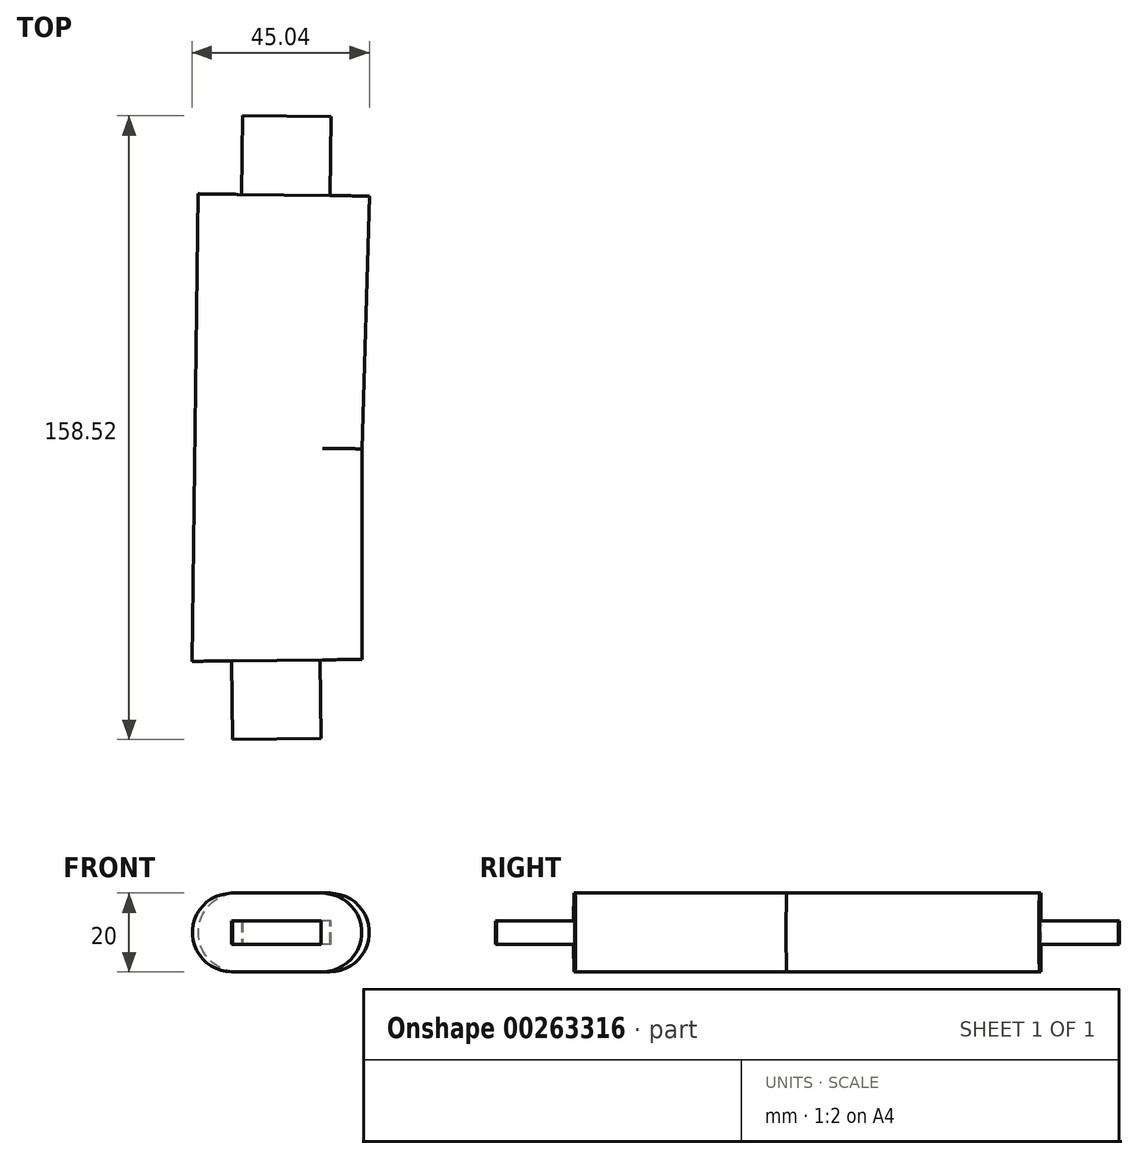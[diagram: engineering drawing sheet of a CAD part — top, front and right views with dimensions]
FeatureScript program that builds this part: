
annotation { "Feature Type Name" : "Feature", "Feature Type Description" : "" }
export const myFeature = defineFeature(function(context is Context, id is Id, definition is map)
    precondition{}
    {
        {
            var Q0;
            Q0=qCreatedBy(makeId("Top.planeOp"),FACE);
            var sketch = newSketch(context, id + "F0", { "sketchPlane" : qUnion([Q0])});
            skArc(sketch, "E0", {"start": v(-69.56, -48.3) * mm, "mid": v(-88.08, -45.25) * mm, "end": v(-106.8, -43.78) * mm});
            skArc(sketch, "E1", {"start": v(-106.8, -43.78) * mm, "mid": v(-96.39, -62.57) * mm, "end": v(-80.73, -77.27) * mm});
            skArc(sketch, "E2", {"start": v(-80.73, -77.27) * mm, "mid": v(-98.26, -84.7) * mm, "end": v(-114.23, -95.07) * mm});
            skArc(sketch, "E3", {"start": v(-114.23, -95.07) * mm, "mid": v(-98.6, -104.41) * mm, "end": v(-80.73, -107.98) * mm});
            skArc(sketch, "E4", {"start": v(-80.73, -107.98) * mm, "mid": v(-90.04, -123.58) * mm, "end": v(-94.69, -141.13) * mm});
            skArc(sketch, "E5", {"start": v(-94.69, -141.13) * mm, "mid": v(-78.8, -139.7) * mm, "end": v(-63.98, -133.8) * mm});
            skArc(sketch, "E6", {"start": v(-63.98, -133.8) * mm, "mid": v(40.14, -139.24) * mm, "end": v(30.94, -35.4) * mm});
            skArc(sketch, "E7", {"start": v(-31.41, -22.87) * mm, "mid": v(-53.17, -31.57) * mm, "end": v(-69.56, -48.3) * mm});
            skCircle(sketch, "E8", {"center": v(-12, -90) * mm, "radius": 35 * mm});
            skLineSegment(sketch, "E9", {"start": v(-12, -90) * mm, "end": v(-12, 0) * mm});
            skLineSegment(sketch, "E10", {"start": v(-12, 0) * mm, "end": v(0, 0) * mm});
            skLineSegment(sketch, "E11", {"start": v(-31.41, -22.87) * mm, "end": v(-12, 0) * mm});
            skLineSegment(sketch, "E12", {"start": v(-31.41, -22.87) * mm, "end": v(0, 0) * mm});
            skArc(sketch, "E13", {"start": v(30.94, -35.4) * mm, "mid": v(57.65, 8.29) * mm, "end": v(64.82, 58.99) * mm});
            skLineSegment(sketch, "E14", {"start": v(64.82, 42.9) * mm, "end": v(70.1, 125.75) * mm});
            skLineSegment(sketch, "E15", {"start": v(70.1, 125.75) * mm, "end": v(73.47, 146.99) * mm});
            skLineSegment(sketch, "E16", {"start": v(73.47, 146.99) * mm, "end": v(91.25, 150.97) * mm});
            skArc(sketch, "E17", {"start": v(93.55, 168.05) * mm, "mid": v(98.13, 170.3) * mm, "end": v(101.04, 174.5) * mm});
            skArc(sketch, "E18", {"start": v(101.04, 174.5) * mm, "mid": v(98.19, 178.86) * mm, "end": v(93.55, 181.22) * mm});
            skArc(sketch, "E19", {"start": v(91.25, 150.97) * mm, "mid": v(97.19, 153.5) * mm, "end": v(101.85, 157.96) * mm});
            skArc(sketch, "E20", {"start": v(101.85, 157.96) * mm, "mid": v(99.5, 164.5) * mm, "end": v(93.55, 168.05) * mm});
            skArc(sketch, "E21", {"start": v(93.55, 181.22) * mm, "mid": v(100.45, 185.24) * mm, "end": v(104.38, 192.2) * mm});
            skArc(sketch, "E22", {"start": v(16.27, 5.35) * mm, "mid": v(27.94, 20.47) * mm, "end": v(35.96, 37.8) * mm});
            skLineSegment(sketch, "E23", {"start": v(16.27, 5.35) * mm, "end": v(12.02, 0.97) * mm});
            skLineSegment(sketch, "E24", {"start": v(12.02, 54.47) * mm, "end": v(16.98, 220.58) * mm});
            skLineSegment(sketch, "E25", {"start": v(16.98, 220.58) * mm, "end": v(16.98, 230.48) * mm});
            skArc(sketch, "E26", {"start": v(20.74, 234.78) * mm, "mid": v(18.05, 233.34) * mm, "end": v(16.98, 230.48) * mm});
            skLineSegment(sketch, "E27", {"start": v(20.74, 234.78) * mm, "end": v(55.67, 234.78) * mm});
            skArc(sketch, "E28", {"start": v(55.67, 234.78) * mm, "mid": v(75.45, 242.82) * mm, "end": v(84, 262.38) * mm});
            skArc(sketch, "E29", {"start": v(84, 262.38) * mm, "mid": v(83.8, 275) * mm, "end": v(79.59, 286.9) * mm});
            skArc(sketch, "E30", {"start": v(79.59, 286.9) * mm, "mid": v(90.12, 305.47) * mm, "end": v(96.46, 325.87) * mm});
            skArc(sketch, "E31", {"start": v(96.46, 325.87) * mm, "mid": v(80.34, 314.22) * mm, "end": v(65.52, 300.95) * mm});
            skArc(sketch, "E32", {"start": v(65.52, 300.95) * mm, "mid": v(66.02, 314.82) * mm, "end": v(65.52, 328.68) * mm});
            skArc(sketch, "E33", {"start": v(41.86, 304.54) * mm, "mid": v(40.03, 315.53) * mm, "end": v(35.9, 325.87) * mm});
            skArc(sketch, "E34", {"start": v(35.9, 325.87) * mm, "mid": v(29.68, 316.4) * mm, "end": v(23.68, 306.81) * mm});
            skArc(sketch, "E35", {"start": v(23.68, 306.81) * mm, "mid": v(-21.12, 284.92) * mm, "end": v(-28, 235.53) * mm});
            skLineSegment(sketch, "E36", {"start": v(-31.41, -22.87) * mm, "end": v(-28, 235.53) * mm});
            skLineSegment(sketch, "E37", {"start": v(0, 0) * mm, "end": v(0, 302.13) * mm});
            skLineSegment(sketch, "E38", {"start": v(12.02, 0.97) * mm, "end": v(-31.41, -22.87) * mm});
            skLineSegment(sketch, "E39", {"start": v(0, 0) * mm, "end": v(12.02, 0.97) * mm});
            skLineSegment(sketch, "E40", {"start": v(12.02, 0.97) * mm, "end": v(30.94, -35.4) * mm});
            skLineSegment(sketch, "E41", {"start": v(64.82, 58.99) * mm, "end": v(46.6, 104.17) * mm});
            skLineSegment(sketch, "E42", {"start": v(12.02, 0.97) * mm, "end": v(12.02, 54.47) * mm});
            skLineSegment(sketch, "E43", {"start": v(-29.54, 119.27) * mm, "end": v(13.94, 118.7) * mm});
            skLineSegment(sketch, "E44", {"start": v(35.96, 37.8) * mm, "end": v(38.97, 138.47) * mm});
            skArc(sketch, "E45", {"start": v(104.38, 192.2) * mm, "mid": v(74.78, 206.52) * mm, "end": v(46.71, 189.39) * mm});
            skArc(sketch, "E46", {"start": v(46.71, 189.39) * mm, "mid": v(41.3, 164.16) * mm, "end": v(38.97, 138.47) * mm});
            skLineSegment(sketch, "E47", {"start": v(104.38, 192.2) * mm, "end": v(93.55, 181.22) * mm});
            skLineSegment(sketch, "E48", {"start": v(93.55, 168.05) * mm, "end": v(101.85, 157.96) * mm});
            skLineSegment(sketch, "E49", {"start": v(93.55, 181.22) * mm, "end": v(101.04, 174.5) * mm});
            skLineSegment(sketch, "E50", {"start": v(93.55, 168.05) * mm, "end": v(101.04, 174.5) * mm});
            skLineSegment(sketch, "E51", {"start": v(41.86, 304.54) * mm, "end": v(65.52, 328.68) * mm});
            skLineSegment(sketch, "E52", {"start": v(16.98, 230.48) * mm, "end": v(-28.07, 230.48) * mm});
            skLineSegment(sketch, "E53", {"start": v(12.02, 0.97) * mm, "end": v(-31.1, 0.49) * mm});
            skPoint(sketch, "E53.endSnap0", {"position": v(6.01, 0.49) * mm});
            skLineSegment(sketch, "E54", {"start": v(12.02, 0.97) * mm, "end": v(43.15, -20.17) * mm});
            skSolve(sketch);
        }
        {
            var Q0;
            {var subQ0=sQuery(id+"F0.wireOp",EDGE,"E38");var subQ1=sQuery(id+"F0.wireOp",EDGE,"E9");var subQ2=makeQuery(id+"F0.imprint","INTERSECT",VERTEX,{"derivedFrom":[subQ1,subQ0]});Q0=makeQuery(id+"F0.imprint","IMPRINT",FACE,{"disambiguationData":[TD([[makeQuery(id+"F0.imprint","IMPRINT",EDGE,{"disambiguationData":[TD([[subQ2,-1.0]])],"derivedFrom":subQ1}),1.0]])]});}
            var Q1;
            {var subQ0=sQuery(id+"F0.wireOp",EDGE,"E11");Q1=makeQuery(id+"F0.imprint","IMPRINT",FACE,{"disambiguationData":[TD([[makeQuery(id+"F0.imprint","IMPRINT",EDGE,{"derivedFrom":subQ0}),-1.0]])]});}
            var Q2;
            {var subQ0=sQuery(id+"F0.wireOp",EDGE,"E39");Q2=makeQuery(id+"F0.imprint","IMPRINT",FACE,{"disambiguationData":[TD([[makeQuery(id+"F0.imprint","IMPRINT",EDGE,{"derivedFrom":subQ0}),1.0]])]});}
            var Q3;
            Q3=makeQuery(id+"F0.imprint","IMPRINT",FACE,{"disambiguationData":[TD([[makeQuery(id+"F0.imprint","IMPRINT",EDGE,{"derivedFrom":sQuery(id+"F0.wireOp",EDGE,"E0")}),1.0]])]});
            var Q4;
            {var subQ5=sQuery(id+"F0.wireOp",EDGE,"E39");Q4=makeQuery(id+"F0.imprint","IMPRINT",FACE,{"disambiguationData":[TD([[makeQuery(id+"F0.imprint","IMPRINT",EDGE,{"derivedFrom":subQ5}),-1.0]])]});}
            var Q5;
            {var subQ2=sQuery(id+"F0.wireOp",EDGE,"E10");Q5=makeQuery(id+"F0.imprint","IMPRINT",FACE,{"disambiguationData":[TD([[makeQuery(id+"F0.imprint","IMPRINT",EDGE,{"derivedFrom":subQ2}),1.0]])]});}
            var Q6;
            {var subQ0=sQuery(id+"F0.wireOp",EDGE,"E10");Q6=makeQuery(id+"F0.imprint","IMPRINT",FACE,{"disambiguationData":[TD([[makeQuery(id+"F0.imprint","IMPRINT",EDGE,{"derivedFrom":subQ0}),-1.0]])]});}
            var Q7;
            {var subQ0=sQuery(id+"F0.wireOp",EDGE,"E40");Q7=makeQuery(id+"F0.imprint","IMPRINT",FACE,{"disambiguationData":[TD([[makeQuery(id+"F0.imprint","IMPRINT",EDGE,{"derivedFrom":subQ0}),1.0]])]});}
            extrude(context, id + "F1", {"entities" : qUnion([Q0, Q1, Q2, Q3, Q4, Q5, Q6, Q7]), "depth" : 20 * mm});
        }
        {
            var Q0;
            {var subQ1=sQuery(id+"F0.wireOp",EDGE,"E14");Q0=makeQuery(id+"F0.imprint","IMPRINT",FACE,{"disambiguationData":[TD([[makeQuery(id+"F0.imprint","IMPRINT",EDGE,{"derivedFrom":subQ1}),1.0]])]});}
            extrude(context, id + "F2", {"entities" : qUnion([Q0]), "depth" : 20 * mm});
        }
        {
            var Q0;
            {var subQ0=sQuery(id+"F0.wireOp",EDGE,"E43");var subQ1=sQuery(id+"F0.wireOp",EDGE,"E36");var subQ2=makeQuery(id+"F0.imprint","INTERSECT",VERTEX,{"derivedFrom":[subQ1,subQ0]});Q0=makeQuery(id+"F0.imprint","IMPRINT",FACE,{"disambiguationData":[TD([[makeQuery(id+"F0.imprint","IMPRINT",EDGE,{"disambiguationData":[TD([[subQ2,1.0]])],"derivedFrom":subQ1}),-1.0]])]});}
            var Q1;
            {var subQ5=sQuery(id+"F0.wireOp",EDGE,"E42");Q1=makeQuery(id+"F0.imprint","IMPRINT",FACE,{"disambiguationData":[TD([[makeQuery(id+"F0.imprint","IMPRINT",EDGE,{"derivedFrom":subQ5}),1.0]])]});}
            extrude(context, id + "F3", {"entities" : qUnion([Q0, Q1]), "depth" : 20 * mm});
        }
        {
            var Q0;
            {var subQ0=sQuery(id+"F0.wireOp",EDGE,"E36");var subQ1=sQuery(id+"F0.wireOp",EDGE,"E35");var subQ2=makeQuery(id+"F0.imprint","INTERSECT",VERTEX,{"derivedFrom":[subQ1,subQ0]});Q0=makeQuery(id+"F0.imprint","IMPRINT",FACE,{"disambiguationData":[TD([[makeQuery(id+"F0.imprint","IMPRINT",EDGE,{"disambiguationData":[TD([[subQ2,1.0]])],"derivedFrom":subQ1}),1.0]])]});}
            var Q1;
            {var subQ4=sQuery(id+"F0.wireOp",EDGE,"E26");Q1=makeQuery(id+"F0.imprint","IMPRINT",FACE,{"disambiguationData":[TD([[makeQuery(id+"F0.imprint","IMPRINT",EDGE,{"derivedFrom":subQ4}),-1.0]])]});}
            extrude(context, id + "F4", {"entities" : qUnion([Q0, Q1]), "depth" : 20 * mm});
        }
        {
            var Q0;
            {var subQ0=sQuery(id+"F0.wireOp",EDGE,"E43");var subQ1=sQuery(id+"F0.wireOp",EDGE,"E36");var subQ2=makeQuery(id+"F0.imprint","INTERSECT",VERTEX,{"derivedFrom":[subQ1,subQ0]});Q0=makeQuery(id+"F0.imprint","IMPRINT",FACE,{"disambiguationData":[TD([[makeQuery(id+"F0.imprint","IMPRINT",EDGE,{"disambiguationData":[TD([[subQ2,-1.0]])],"derivedFrom":subQ1}),-1.0]])]});}
            var Q1;
            {var subQ7=sQuery(id+"F0.wireOp",EDGE,"E25");Q1=makeQuery(id+"F0.imprint","IMPRINT",FACE,{"disambiguationData":[TD([[makeQuery(id+"F0.imprint","IMPRINT",EDGE,{"derivedFrom":subQ7}),1.0]])]});}
            extrude(context, id + "F5", {"entities" : qUnion([Q0, Q1]), "depth" : 20 * mm});
        }
        {
            var Q0;
            Q0=makeQuery(id+"F1.opExtrude","CAP_EDGE",EDGE,{"disambiguationData":[OSD([sQuery(id+"F0.wireOp",EDGE,"E36")])],"isStart":false});
            var Q1;
            Q1=makeQuery(id+"F1.opExtrude","CAP_EDGE",EDGE,{"disambiguationData":[OSD([sQuery(id+"F0.wireOp",EDGE,"E24")])],"isStart":false});
            var Q2;
            Q2=makeQuery(id+"F1.opExtrude","CAP_EDGE",EDGE,{"disambiguationData":[OSD([sQuery(id+"F0.wireOp",EDGE,"E42")])],"isStart":false});
            var Q3;
            Q3=makeQuery(id+"F1.opExtrude","CAP_EDGE",EDGE,{"disambiguationData":[OSD([sQuery(id+"F0.wireOp",EDGE,"E25")])],"isStart":false});
            var Q4;
            Q4=makeQuery(id+"F1.opExtrude","CAP_EDGE",EDGE,{"disambiguationData":[OSD([sQuery(id+"F0.wireOp",EDGE,"E35")])],"isStart":false});
            var Q5;
            Q5=makeQuery(id+"F1.opExtrude","CAP_EDGE",EDGE,{"disambiguationData":[OSD([sQuery(id+"F0.wireOp",EDGE,"E26")])],"isStart":false});
            var Q6;
            Q6=makeQuery(id+"F1.opExtrude","CAP_EDGE",EDGE,{"disambiguationData":[OSD([sQuery(id+"F0.wireOp",EDGE,"E42")])],"isStart":true});
            var Q7;
            Q7=makeQuery(id+"F1.opExtrude","CAP_EDGE",EDGE,{"disambiguationData":[OSD([sQuery(id+"F0.wireOp",EDGE,"E25")])],"isStart":true});
            var Q8;
            Q8=makeQuery(id+"F1.opExtrude","CAP_EDGE",EDGE,{"disambiguationData":[OSD([sQuery(id+"F0.wireOp",EDGE,"E36")])],"isStart":true});
            var Q9;
            Q9=makeQuery(id+"F1.opExtrude","CAP_EDGE",EDGE,{"disambiguationData":[OSD([sQuery(id+"F0.wireOp",EDGE,"E35")])],"isStart":true});
            var Q10;
            Q10=makeQuery(id+"F1.opExtrude","CAP_EDGE",EDGE,{"disambiguationData":[OSD([sQuery(id+"F0.wireOp",EDGE,"E26")])],"isStart":true});
            var Q11;
            Q11=makeQuery(id+"F1.opExtrude","CAP_EDGE",EDGE,{"disambiguationData":[OSD([sQuery(id+"F0.wireOp",EDGE,"E22")])],"isStart":false});
            var Q12;
            Q12=makeQuery(id+"F1.opExtrude","CAP_EDGE",EDGE,{"disambiguationData":[OSD([sQuery(id+"F0.wireOp",EDGE,"E23")])],"isStart":false});
            var Q13;
            Q13=makeQuery(id+"F1.opExtrude","CAP_EDGE",EDGE,{"disambiguationData":[OSD([sQuery(id+"F0.wireOp",EDGE,"E44")])],"isStart":false});
            var Q14;
            Q14=makeQuery(id+"F1.opExtrude","CAP_EDGE",EDGE,{"disambiguationData":[OSD([sQuery(id+"F0.wireOp",EDGE,"E45")])],"isStart":false});
            var Q15;
            Q15=makeQuery(id+"F1.opExtrude","CAP_EDGE",EDGE,{"disambiguationData":[OSD([sQuery(id+"F0.wireOp",EDGE,"E22")])],"isStart":true});
            var Q16;
            Q16=makeQuery(id+"F1.opExtrude","CAP_EDGE",EDGE,{"disambiguationData":[OSD([sQuery(id+"F0.wireOp",EDGE,"E44")])],"isStart":true});
            var Q17;
            Q17=makeQuery(id+"F1.opExtrude","CAP_EDGE",EDGE,{"disambiguationData":[OSD([sQuery(id+"F0.wireOp",EDGE,"E45")])],"isStart":true});
            var Q18;
            Q18=makeQuery(id+"F1.opExtrude","CAP_EDGE",EDGE,{"disambiguationData":[OSD([sQuery(id+"F0.wireOp",EDGE,"E13")])],"isStart":false});
            var Q19;
            Q19=makeQuery(id+"F1.opExtrude","CAP_EDGE",EDGE,{"disambiguationData":[OSD([sQuery(id+"F0.wireOp",EDGE,"E14")])],"isStart":false});
            var Q20;
            Q20=makeQuery(id+"F1.opExtrude","CAP_EDGE",EDGE,{"disambiguationData":[OSD([sQuery(id+"F0.wireOp",EDGE,"E15")])],"isStart":false});
            var Q21;
            Q21=makeQuery(id+"F1.opExtrude","CAP_EDGE",EDGE,{"disambiguationData":[OSD([sQuery(id+"F0.wireOp",EDGE,"E16")])],"isStart":false});
            var Q22;
            Q22=makeQuery(id+"F1.opExtrude","CAP_EDGE",EDGE,{"disambiguationData":[OSD([sQuery(id+"F0.wireOp",EDGE,"E16")])],"isStart":true});
            var Q23;
            Q23=makeQuery(id+"F1.opExtrude","CAP_EDGE",EDGE,{"disambiguationData":[OSD([sQuery(id+"F0.wireOp",EDGE,"E15")])],"isStart":true});
            var Q24;
            Q24=makeQuery(id+"F1.opExtrude","CAP_EDGE",EDGE,{"disambiguationData":[OSD([sQuery(id+"F0.wireOp",EDGE,"E14")])],"isStart":true});
            var Q25;
            Q25=makeQuery(id+"F1.opExtrude","CAP_EDGE",EDGE,{"disambiguationData":[OSD([sQuery(id+"F0.wireOp",EDGE,"E13")])],"isStart":true});
            var Q26;
            Q26=makeQuery(id+"F1.opExtrude","CAP_EDGE",EDGE,{"disambiguationData":[OSD([sQuery(id+"F0.wireOp",EDGE,"E6")])],"isStart":false});
            var Q27;
            Q27=makeQuery(id+"F1.opExtrude","CAP_EDGE",EDGE,{"disambiguationData":[OSD([sQuery(id+"F0.wireOp",EDGE,"E8")])],"isStart":false});
            var Q28;
            Q28=makeQuery(id+"F1.opExtrude","CAP_EDGE",EDGE,{"disambiguationData":[OSD([sQuery(id+"F0.wireOp",EDGE,"E7")])],"isStart":false});
            var Q29;
            Q29=makeQuery(id+"F1.opExtrude","CAP_EDGE",EDGE,{"disambiguationData":[OSD([sQuery(id+"F0.wireOp",EDGE,"E8")])],"isStart":true});
            var Q30;
            Q30=makeQuery(id+"F1.opExtrude","CAP_EDGE",EDGE,{"disambiguationData":[OSD([sQuery(id+"F0.wireOp",EDGE,"E7")])],"isStart":true});
            var Q31;
            Q31=makeQuery(id+"F1.opExtrude","CAP_EDGE",EDGE,{"disambiguationData":[OSD([sQuery(id+"F0.wireOp",EDGE,"E6")])],"isStart":true});
            fillet(context, id + "F6", {"entities" : qUnion([Q0, Q1, Q2, Q3, Q4, Q5, Q6, Q7, Q8, Q9, Q10, Q11, Q12, Q13, Q14, Q15, Q16, Q17, Q18, Q19, Q20, Q21, Q22, Q23, Q24, Q25, Q26, Q27, Q28, Q29, Q30, Q31]), "radius" : 10 * mm, "tangentPropagation" : true, "allowEdgeOverflow" : false});
        }
        {
            var Q0;
            Q0=makeQuery(id+"F1.opExtrude","CAP_EDGE",EDGE,{"disambiguationData":[OSD([sQuery(id+"F0.wireOp",EDGE,"E0")])],"isStart":false});
            var Q1;
            Q1=makeQuery(id+"F1.opExtrude","CAP_EDGE",EDGE,{"disambiguationData":[OSD([sQuery(id+"F0.wireOp",EDGE,"E1")])],"isStart":false});
            var Q2;
            Q2=makeQuery(id+"F1.opExtrude","CAP_EDGE",EDGE,{"disambiguationData":[OSD([sQuery(id+"F0.wireOp",EDGE,"E5")])],"isStart":false});
            var Q3;
            Q3=makeQuery(id+"F1.opExtrude","CAP_EDGE",EDGE,{"disambiguationData":[OSD([sQuery(id+"F0.wireOp",EDGE,"E4")])],"isStart":false});
            var Q4;
            Q4=makeQuery(id+"F1.opExtrude","CAP_EDGE",EDGE,{"disambiguationData":[OSD([sQuery(id+"F0.wireOp",EDGE,"E0")])],"isStart":true});
            var Q5;
            Q5=makeQuery(id+"F1.opExtrude","CAP_EDGE",EDGE,{"disambiguationData":[OSD([sQuery(id+"F0.wireOp",EDGE,"E1")])],"isStart":true});
            var Q6;
            Q6=makeQuery(id+"F1.opExtrude","CAP_EDGE",EDGE,{"disambiguationData":[OSD([sQuery(id+"F0.wireOp",EDGE,"E4")])],"isStart":true});
            var Q7;
            Q7=makeQuery(id+"F1.opExtrude","CAP_EDGE",EDGE,{"disambiguationData":[OSD([sQuery(id+"F0.wireOp",EDGE,"E5")])],"isStart":true});
            fillet(context, id + "F7", {"entities" : qUnion([Q0, Q1, Q2, Q3, Q4, Q5, Q6, Q7]), "radius" : 9.5 * mm, "tangentPropagation" : true, "rho" : 0.5, "crossSection" : FilletCrossSection.CONIC, "allowEdgeOverflow" : false});
        }
        {
            var Q0;
            Q0=makeQuery(id+"F1.opExtrude","CAP_EDGE",EDGE,{"disambiguationData":[OSD([sQuery(id+"F0.wireOp",EDGE,"E3")])],"isStart":true});
            var Q1;
            Q1=makeQuery(id+"F1.opExtrude","CAP_EDGE",EDGE,{"disambiguationData":[OSD([sQuery(id+"F0.wireOp",EDGE,"E2")])],"isStart":true});
            var Q2;
            Q2=makeQuery(id+"F1.opExtrude","CAP_EDGE",EDGE,{"disambiguationData":[OSD([sQuery(id+"F0.wireOp",EDGE,"E2")])],"isStart":false});
            var Q3;
            Q3=makeQuery(id+"F1.opExtrude","CAP_EDGE",EDGE,{"disambiguationData":[OSD([sQuery(id+"F0.wireOp",EDGE,"E3")])],"isStart":false});
            fillet(context, id + "F8", {"entities" : qUnion([Q0, Q1, Q2, Q3]), "radius" : 3 * mm, "tangentPropagation" : true, "allowEdgeOverflow" : false});
        }
        {
            var Q0;
            Q0=makeQuery(id+"F2.opExtrude","CAP_EDGE",EDGE,{"disambiguationData":[OSD([sQuery(id+"F0.wireOp",EDGE,"E14")])],"isStart":false});
            var Q1;
            Q1=makeQuery(id+"F2.opExtrude","CAP_EDGE",EDGE,{"disambiguationData":[OSD([sQuery(id+"F0.wireOp",EDGE,"E15")])],"isStart":false});
            var Q2;
            Q2=makeQuery(id+"F2.opExtrude","CAP_EDGE",EDGE,{"disambiguationData":[OSD([sQuery(id+"F0.wireOp",EDGE,"E14")])],"isStart":true});
            var Q3;
            Q3=makeQuery(id+"F2.opExtrude","CAP_EDGE",EDGE,{"disambiguationData":[OSD([sQuery(id+"F0.wireOp",EDGE,"E15")])],"isStart":true});
            var Q4;
            Q4=makeQuery(id+"F2.opExtrude","CAP_EDGE",EDGE,{"disambiguationData":[OSD([sQuery(id+"F0.wireOp",EDGE,"E16")])],"isStart":true});
            var Q5;
            Q5=makeQuery(id+"F2.opExtrude","CAP_EDGE",EDGE,{"disambiguationData":[OSD([sQuery(id+"F0.wireOp",EDGE,"E16")])],"isStart":false});
            var Q6;
            Q6=makeQuery(id+"F2.opExtrude","CAP_EDGE",EDGE,{"disambiguationData":[OSD([sQuery(id+"F0.wireOp",EDGE,"E45")])],"isStart":true});
            var Q7;
            Q7=makeQuery(id+"F2.opExtrude","CAP_EDGE",EDGE,{"disambiguationData":[OSD([sQuery(id+"F0.wireOp",EDGE,"E45")])],"isStart":false});
            var Q8;
            Q8=makeQuery(id+"F2.opExtrude","CAP_EDGE",EDGE,{"disambiguationData":[OSD([sQuery(id+"F0.wireOp",EDGE,"E46")])],"isStart":false});
            var Q9;
            Q9=makeQuery(id+"F2.opExtrude","CAP_EDGE",EDGE,{"disambiguationData":[OSD([sQuery(id+"F0.wireOp",EDGE,"E44")])],"isStart":false});
            var Q10;
            Q10=makeQuery(id+"F2.opExtrude","CAP_EDGE",EDGE,{"disambiguationData":[OSD([sQuery(id+"F0.wireOp",EDGE,"E22")])],"isStart":false});
            var Q11;
            Q11=makeQuery(id+"F2.opExtrude","CAP_EDGE",EDGE,{"disambiguationData":[OSD([sQuery(id+"F0.wireOp",EDGE,"E23")])],"isStart":false});
            var Q12;
            Q12=makeQuery(id+"F2.opExtrude","CAP_EDGE",EDGE,{"disambiguationData":[OSD([sQuery(id+"F0.wireOp",EDGE,"E46")])],"isStart":true});
            var Q13;
            Q13=makeQuery(id+"F2.opExtrude","CAP_EDGE",EDGE,{"disambiguationData":[OSD([sQuery(id+"F0.wireOp",EDGE,"E23")])],"isStart":true});
            var Q14;
            Q14=makeQuery(id+"F2.opExtrude","CAP_EDGE",EDGE,{"disambiguationData":[OSD([sQuery(id+"F0.wireOp",EDGE,"E22")])],"isStart":true});
            var Q15;
            Q15=makeQuery(id+"F2.opExtrude","CAP_EDGE",EDGE,{"disambiguationData":[OSD([sQuery(id+"F0.wireOp",EDGE,"E44")])],"isStart":true});
            var Q16;
            Q16=makeQuery(id+"F3.opExtrude","CAP_EDGE",EDGE,{"disambiguationData":[OSD([sQuery(id+"F0.wireOp",EDGE,"E24")])],"isStart":false});
            var Q17;
            Q17=makeQuery(id+"F3.opExtrude","CAP_EDGE",EDGE,{"disambiguationData":[OSD([sQuery(id+"F0.wireOp",EDGE,"E42")])],"isStart":false});
            var Q18;
            Q18=makeQuery(id+"F3.opExtrude","CAP_EDGE",EDGE,{"disambiguationData":[OSD([sQuery(id+"F0.wireOp",EDGE,"E42")])],"isStart":true});
            var Q19;
            Q19=makeQuery(id+"F3.opExtrude","CAP_EDGE",EDGE,{"disambiguationData":[OSD([sQuery(id+"F0.wireOp",EDGE,"E24")])],"isStart":true});
            var Q20;
            Q20=makeQuery(id+"F3.opExtrude","CAP_EDGE",EDGE,{"disambiguationData":[OSD([sQuery(id+"F0.wireOp",EDGE,"E25")])],"isStart":true});
            var Q21;
            Q21=makeQuery(id+"F3.opExtrude","CAP_EDGE",EDGE,{"disambiguationData":[OSD([sQuery(id+"F0.wireOp",EDGE,"E36")])],"isStart":false});
            var Q22;
            Q22=makeQuery(id+"F3.opExtrude","CAP_EDGE",EDGE,{"disambiguationData":[OSD([sQuery(id+"F0.wireOp",EDGE,"E36")])],"isStart":true});
            var Q23;
            Q23=makeQuery(id+"F4.opExtrude","CAP_EDGE",EDGE,{"disambiguationData":[OSD([sQuery(id+"F0.wireOp",EDGE,"E36")])],"isStart":true});
            var Q24;
            Q24=makeQuery(id+"F4.opExtrude","CAP_EDGE",EDGE,{"disambiguationData":[OSD([sQuery(id+"F0.wireOp",EDGE,"E36")])],"isStart":false});
            var Q25;
            Q25=makeQuery(id+"F4.opExtrude","CAP_EDGE",EDGE,{"disambiguationData":[OSD([sQuery(id+"F0.wireOp",EDGE,"E35")])],"isStart":true});
            var Q26;
            Q26=makeQuery(id+"F4.opExtrude","CAP_EDGE",EDGE,{"disambiguationData":[OSD([sQuery(id+"F0.wireOp",EDGE,"E35")])],"isStart":false});
            var Q27;
            Q27=makeQuery(id+"F4.opExtrude","CAP_EDGE",EDGE,{"disambiguationData":[OSD([sQuery(id+"F0.wireOp",EDGE,"E27")])],"isStart":false});
            var Q28;
            Q28=makeQuery(id+"F4.opExtrude","CAP_EDGE",EDGE,{"disambiguationData":[OSD([sQuery(id+"F0.wireOp",EDGE,"E28")])],"isStart":false});
            var Q29;
            Q29=makeQuery(id+"F4.opExtrude","CAP_EDGE",EDGE,{"disambiguationData":[OSD([sQuery(id+"F0.wireOp",EDGE,"E29")])],"isStart":false});
            var Q30;
            Q30=makeQuery(id+"F4.opExtrude","CAP_EDGE",EDGE,{"disambiguationData":[OSD([sQuery(id+"F0.wireOp",EDGE,"E27")])],"isStart":true});
            var Q31;
            Q31=makeQuery(id+"F4.opExtrude","CAP_EDGE",EDGE,{"disambiguationData":[OSD([sQuery(id+"F0.wireOp",EDGE,"E28")])],"isStart":true});
            var Q32;
            Q32=makeQuery(id+"F4.opExtrude","CAP_EDGE",EDGE,{"disambiguationData":[OSD([sQuery(id+"F0.wireOp",EDGE,"E29")])],"isStart":true});
            var Q33;
            Q33=makeQuery(id+"F4.opExtrude","CAP_EDGE",EDGE,{"disambiguationData":[OSD([sQuery(id+"F0.wireOp",EDGE,"E26")])],"isStart":false});
            var Q34;
            Q34=makeQuery(id+"F4.opExtrude","CAP_EDGE",EDGE,{"disambiguationData":[OSD([sQuery(id+"F0.wireOp",EDGE,"E26")])],"isStart":true});
            var Q35;
            Q35=makeQuery(id+"F4.opExtrude","CAP_EDGE",EDGE,{"disambiguationData":[OSD([sQuery(id+"F0.wireOp",EDGE,"E30")])],"isStart":false});
            var Q36;
            Q36=makeQuery(id+"F4.opExtrude","CAP_EDGE",EDGE,{"disambiguationData":[OSD([sQuery(id+"F0.wireOp",EDGE,"E31")])],"isStart":false});
            var Q37;
            Q37=makeQuery(id+"F4.opExtrude","CAP_EDGE",EDGE,{"disambiguationData":[OSD([sQuery(id+"F0.wireOp",EDGE,"E30")])],"isStart":true});
            var Q38;
            Q38=makeQuery(id+"F4.opExtrude","CAP_EDGE",EDGE,{"disambiguationData":[OSD([sQuery(id+"F0.wireOp",EDGE,"E31")])],"isStart":true});
            var Q39;
            Q39=makeQuery(id+"F4.opExtrude","CAP_EDGE",EDGE,{"disambiguationData":[OSD([sQuery(id+"F0.wireOp",EDGE,"E33")])],"isStart":false});
            var Q40;
            Q40=makeQuery(id+"F4.opExtrude","CAP_EDGE",EDGE,{"disambiguationData":[OSD([sQuery(id+"F0.wireOp",EDGE,"E34")])],"isStart":false});
            var Q41;
            Q41=makeQuery(id+"F4.opExtrude","CAP_EDGE",EDGE,{"disambiguationData":[OSD([sQuery(id+"F0.wireOp",EDGE,"E34")])],"isStart":true});
            var Q42;
            Q42=makeQuery(id+"F4.opExtrude","CAP_EDGE",EDGE,{"disambiguationData":[OSD([sQuery(id+"F0.wireOp",EDGE,"E33")])],"isStart":true});
            var Q43;
            Q43=makeQuery(id+"F5.opExtrude","CAP_EDGE",EDGE,{"disambiguationData":[OSD([sQuery(id+"F0.wireOp",EDGE,"E36")])],"isStart":true});
            var Q44;
            Q44=makeQuery(id+"F5.opExtrude","CAP_EDGE",EDGE,{"disambiguationData":[OSD([sQuery(id+"F0.wireOp",EDGE,"E24")])],"isStart":true});
            var Q45;
            Q45=makeQuery(id+"F5.opExtrude","CAP_EDGE",EDGE,{"disambiguationData":[OSD([sQuery(id+"F0.wireOp",EDGE,"E36")])],"isStart":false});
            var Q46;
            Q46=makeQuery(id+"F5.opExtrude","CAP_EDGE",EDGE,{"disambiguationData":[OSD([sQuery(id+"F0.wireOp",EDGE,"E24")])],"isStart":false});
            fillet(context, id + "F9", {"entities" : qUnion([Q0, Q1, Q2, Q3, Q4, Q5, Q6, Q7, Q8, Q9, Q10, Q11, Q12, Q13, Q14, Q15, Q16, Q17, Q18, Q19, Q20, Q21, Q22, Q23, Q24, Q25, Q26, Q27, Q28, Q29, Q30, Q31, Q32, Q33, Q34, Q35, Q36, Q37, Q38, Q39, Q40, Q41, Q42, Q43, Q44, Q45, Q46]), "radius" : 10 * mm, "tangentPropagation" : true, "allowEdgeOverflow" : false});
        }
        {
            var Q0;
            Q0=makeQuery(id+"F4.opExtrude","CAP_EDGE",EDGE,{"disambiguationData":[OSD([sQuery(id+"F0.wireOp",EDGE,"E51")])],"isStart":false});
            var Q1;
            Q1=makeQuery(id+"F4.opExtrude","CAP_EDGE",EDGE,{"disambiguationData":[OSD([sQuery(id+"F0.wireOp",EDGE,"E32")])],"isStart":false});
            var Q2;
            Q2=makeQuery(id+"F4.opExtrude","CAP_EDGE",EDGE,{"disambiguationData":[OSD([sQuery(id+"F0.wireOp",EDGE,"E32")])],"isStart":true});
            var Q3;
            Q3=makeQuery(id+"F4.opExtrude","CAP_EDGE",EDGE,{"disambiguationData":[OSD([sQuery(id+"F0.wireOp",EDGE,"E51")])],"isStart":true});
            fillet(context, id + "F10", {"entities" : qUnion([Q0, Q1, Q2, Q3]), "radius" : 5 * mm, "tangentPropagation" : true, "allowEdgeOverflow" : false});
        }
        {
            var Q0;
            Q0=makeQuery(id+"F2.opExtrude","CAP_EDGE",EDGE,{"disambiguationData":[OSD([sQuery(id+"F0.wireOp",EDGE,"E50")])],"isStart":true});
            var Q1;
            Q1=makeQuery(id+"F2.opExtrude","CAP_EDGE",EDGE,{"disambiguationData":[OSD([sQuery(id+"F0.wireOp",EDGE,"E49")])],"isStart":true});
            var Q2;
            Q2=makeQuery(id+"F2.opExtrude","CAP_EDGE",EDGE,{"disambiguationData":[OSD([sQuery(id+"F0.wireOp",EDGE,"E49")])],"isStart":false});
            var Q3;
            Q3=makeQuery(id+"F2.opExtrude","CAP_EDGE",EDGE,{"disambiguationData":[OSD([sQuery(id+"F0.wireOp",EDGE,"E50")])],"isStart":false});
            var Q4;
            Q4=makeQuery(id+"F9.opFillet","BLEND_EDGE",EDGE,{"blendedFrom":[makeQuery(id+"F2.opExtrude","CAP_EDGE",EDGE,{"disambiguationData":[OSD([sQuery(id+"F0.wireOp",EDGE,"E45")])],"isStart":false}),makeQuery(id+"F2.opExtrude","SWEPT_FACE",FACE,{"disambiguationData":[OSD([sQuery(id+"F0.wireOp",EDGE,"E47")])]})],"blendedInto":[makeQuery(id+"F2.opExtrude","SWEPT_FACE",FACE,{"disambiguationData":[OSD([sQuery(id+"F0.wireOp",EDGE,"E47")])]})]});
            var Q5;
            Q5=makeQuery(id+"F9.opFillet","BLEND_EDGE",EDGE,{"blendedFrom":[makeQuery(id+"F2.opExtrude","CAP_EDGE",EDGE,{"disambiguationData":[OSD([sQuery(id+"F0.wireOp",EDGE,"E19")])],"isStart":false}),makeQuery(id+"F2.opExtrude","SWEPT_FACE",FACE,{"disambiguationData":[OSD([sQuery(id+"F0.wireOp",EDGE,"E48")])]})],"blendedInto":[makeQuery(id+"F2.opExtrude","SWEPT_FACE",FACE,{"disambiguationData":[OSD([sQuery(id+"F0.wireOp",EDGE,"E48")])]})]});
            fillet(context, id + "F11", {"entities" : qUnion([Q0, Q1, Q2, Q3, Q4, Q5]), "radius" : 5 * mm, "tangentPropagation" : true, "allowEdgeOverflow" : false});
        }
        {
            var Q0;
            Q0=makeQuery(id+"F6.opFillet","SPLIT",FACE,{"disambiguationData":[OD(0.0)],"derivedFrom":makeQuery(id+"F1.opExtrude","CAP_FACE",FACE,{"disambiguationData":[OSD([sQuery(id+"F0.wireOp",EDGE,"E0"),sQuery(id+"F0.wireOp",EDGE,"E1"),sQuery(id+"F0.wireOp",EDGE,"E2"),sQuery(id+"F0.wireOp",EDGE,"E3"),sQuery(id+"F0.wireOp",EDGE,"E4"),sQuery(id+"F0.wireOp",EDGE,"E5"),sQuery(id+"F0.wireOp",EDGE,"E6"),sQuery(id+"F0.wireOp",EDGE,"E7"),sQuery(id+"F0.wireOp",EDGE,"E8"),sQuery(id+"F0.wireOp",EDGE,"E13"),sQuery(id+"F0.wireOp",EDGE,"E14"),sQuery(id+"F0.wireOp",EDGE,"E15"),sQuery(id+"F0.wireOp",EDGE,"E16"),sQuery(id+"F0.wireOp",EDGE,"E19"),sQuery(id+"F0.wireOp",EDGE,"E22"),sQuery(id+"F0.wireOp",EDGE,"E23"),sQuery(id+"F0.wireOp",EDGE,"E24"),sQuery(id+"F0.wireOp",EDGE,"E25"),sQuery(id+"F0.wireOp",EDGE,"E26"),sQuery(id+"F0.wireOp",EDGE,"E27"),sQuery(id+"F0.wireOp",EDGE,"E28"),sQuery(id+"F0.wireOp",EDGE,"E29"),sQuery(id+"F0.wireOp",EDGE,"E30"),sQuery(id+"F0.wireOp",EDGE,"E31"),sQuery(id+"F0.wireOp",EDGE,"E32"),sQuery(id+"F0.wireOp",EDGE,"E33"),sQuery(id+"F0.wireOp",EDGE,"E34"),sQuery(id+"F0.wireOp",EDGE,"E35"),sQuery(id+"F0.wireOp",EDGE,"E36"),sQuery(id+"F0.wireOp",EDGE,"E42"),sQuery(id+"F0.wireOp",EDGE,"E44"),sQuery(id+"F0.wireOp",EDGE,"E45"),sQuery(id+"F0.wireOp",EDGE,"E46"),sQuery(id+"F0.wireOp",EDGE,"E47"),sQuery(id+"F0.wireOp",EDGE,"E48"),sQuery(id+"F0.wireOp",EDGE,"E49"),sQuery(id+"F0.wireOp",EDGE,"E50"),sQuery(id+"F0.wireOp",EDGE,"E51")])],"isStart":false})});
            var sketch = newSketch(context, id + "F12", { "sketchPlane" : qUnion([Q0])});
            skLineSegment(sketch, "E55", {"start": v(0, 0) * mm, "end": v(3.83, 289.97) * mm});
            skLineSegment(sketch, "E56", {"start": v(3.83, 289.97) * mm, "end": v(19.83, 289.76) * mm});
            skCircle(sketch, "E57", {"center": v(19.83, 289.76) * mm, "radius": 10 * mm});
            skSolve(sketch);
        }
        {
            var Q0;
            Q0=makeQuery(id+"F12.imprint","IMPRINT",FACE,{"disambiguationData":[TD([[makeQuery(id+"F12.imprint","IMPRINT",EDGE,{"derivedFrom":sQuery(id+"F12.wireOp",EDGE,"E57")}),1.0]])]});
            extrude(context, id + "F13", {"entities" : qUnion([Q0]), "operationType" : NewBodyOperationType.ADD, "depth" : 5 * mm, "hasSecondDirection" : true, "secondDirectionOppositeDirection" : true, "secondDirectionDepth" : 25 * mm});
        }
        {
            var Q0;
            Q0=makeQuery(id+"F13.opExtrude","CAP_EDGE",EDGE,{"disambiguationData":[OSD([sQuery(id+"F12.wireOp",EDGE,"E57")])],"isStart":false});
            chamfer(context, id + "F14", {"entities" : qUnion([Q0]), "chamferType" : ChamferType.OFFSET_ANGLE, "width" : 7 * mm, "oppositeDirection" : false, "angle" : 30 * degree, "tangentPropagation" : true});
        }
        {
            var Q0;
            Q0=makeQuery(id+"F13.opExtrude","CAP_EDGE",EDGE,{"disambiguationData":[OSD([sQuery(id+"F12.wireOp",EDGE,"E57")])],"isStart":true});
            chamfer(context, id + "F15", {"entities" : qUnion([Q0]), "chamferType" : ChamferType.OFFSET_ANGLE, "width" : 4 * mm, "oppositeDirection" : false, "angle" : 60 * degree, "tangentPropagation" : true});
        }
        {
            var Q0;
            Q0=makeQuery(id+"F1.opExtrude","SWEPT_BODY",BODY,{"disambiguationData":[OSD([sQuery(id+"F0.wireOp",EDGE,"E0"),sQuery(id+"F0.wireOp",EDGE,"E1"),sQuery(id+"F0.wireOp",EDGE,"E2"),sQuery(id+"F0.wireOp",EDGE,"E3"),sQuery(id+"F0.wireOp",EDGE,"E4"),sQuery(id+"F0.wireOp",EDGE,"E5"),sQuery(id+"F0.wireOp",EDGE,"E6"),sQuery(id+"F0.wireOp",EDGE,"E7"),sQuery(id+"F0.wireOp",EDGE,"E8"),sQuery(id+"F0.wireOp",EDGE,"E13"),sQuery(id+"F0.wireOp",EDGE,"E36"),sQuery(id+"F0.wireOp",EDGE,"E53"),sQuery(id+"F0.wireOp",EDGE,"E54")])]});
            var Q1;
            Q1=makeQuery(id+"F2.opExtrude","SWEPT_BODY",BODY,{"disambiguationData":[OSD([sQuery(id+"F0.wireOp",EDGE,"E13"),sQuery(id+"F0.wireOp",EDGE,"E14"),sQuery(id+"F0.wireOp",EDGE,"E15"),sQuery(id+"F0.wireOp",EDGE,"E16"),sQuery(id+"F0.wireOp",EDGE,"E19"),sQuery(id+"F0.wireOp",EDGE,"E22"),sQuery(id+"F0.wireOp",EDGE,"E23"),sQuery(id+"F0.wireOp",EDGE,"E44"),sQuery(id+"F0.wireOp",EDGE,"E45"),sQuery(id+"F0.wireOp",EDGE,"E46"),sQuery(id+"F0.wireOp",EDGE,"E47"),sQuery(id+"F0.wireOp",EDGE,"E48"),sQuery(id+"F0.wireOp",EDGE,"E49"),sQuery(id+"F0.wireOp",EDGE,"E50"),sQuery(id+"F0.wireOp",EDGE,"E54")])]});
            var Q2;
            Q2=makeQuery(id+"F4.opExtrude","SWEPT_BODY",BODY,{"disambiguationData":[OSD([sQuery(id+"F0.wireOp",EDGE,"E26"),sQuery(id+"F0.wireOp",EDGE,"E27"),sQuery(id+"F0.wireOp",EDGE,"E28"),sQuery(id+"F0.wireOp",EDGE,"E29"),sQuery(id+"F0.wireOp",EDGE,"E30"),sQuery(id+"F0.wireOp",EDGE,"E31"),sQuery(id+"F0.wireOp",EDGE,"E32"),sQuery(id+"F0.wireOp",EDGE,"E33"),sQuery(id+"F0.wireOp",EDGE,"E34"),sQuery(id+"F0.wireOp",EDGE,"E35"),sQuery(id+"F0.wireOp",EDGE,"E36"),sQuery(id+"F0.wireOp",EDGE,"E51"),sQuery(id+"F0.wireOp",EDGE,"E52")])]});
            deleteBodies(context, id + "F16", {"entities" : qUnion([Q0, Q1, Q2])});
        }
        {
            var Q0;
            Q0=makeQuery(id+"F3.opExtrude","SWEPT_FACE",FACE,{"disambiguationData":[OSD([sQuery(id+"F0.wireOp",EDGE,"E53")])]});
            var sketch = newSketch(context, id + "F17", { "sketchPlane" : qUnion([Q0])});
            skLineSegment(sketch, "E58", {"start": v(-31.1, 10) * mm, "end": v(-21.1, 10) * mm});
            skLineSegment(sketch, "E59", {"start": v(-21.1, 10) * mm, "end": v(-21.1, 13) * mm});
            skLineSegment(sketch, "E60.bottom", {"start": v(-21.1, 13) * mm, "end": v(1.4, 13) * mm});
            skLineSegment(sketch, "E60.top", {"start": v(-21.1, 7) * mm, "end": v(1.4, 7) * mm});
            skLineSegment(sketch, "E60.left", {"start": v(-21.1, 13) * mm, "end": v(-21.1, 7) * mm});
            skLineSegment(sketch, "E60.right", {"start": v(1.4, 13) * mm, "end": v(1.4, 7) * mm});
            skSolve(sketch);
        }
        {
            var Q0;
            Q0 = qSketchRegion(id + "F17", true);
            extrude(context, id + "F18", {"entities" : qUnion([Q0]), "operationType" : NewBodyOperationType.ADD, "depth" : 20 * mm});
        }
        {
            var Q0;
            Q0=makeQuery(id+"F5.opExtrude","SWEPT_FACE",FACE,{"disambiguationData":[OSD([sQuery(id+"F0.wireOp",EDGE,"E52")])]});
            var sketch = newSketch(context, id + "F19", { "sketchPlane" : qUnion([Q0])});
            skLineSegment(sketch, "E61", {"start": v(18.07, 10) * mm, "end": v(18.07, 7) * mm});
            skLineSegment(sketch, "E62.bottom", {"start": v(18.07, 7) * mm, "end": v(-4.43, 7) * mm});
            skLineSegment(sketch, "E62.top", {"start": v(18.07, 13) * mm, "end": v(-4.43, 13) * mm});
            skLineSegment(sketch, "E62.left", {"start": v(18.07, 7) * mm, "end": v(18.07, 13) * mm});
            skLineSegment(sketch, "E62.right", {"start": v(-4.43, 7) * mm, "end": v(-4.43, 13) * mm});
            skLineSegment(sketch, "E63", {"start": v(28.07, 10) * mm, "end": v(28.07, 20) * mm});
            skLineSegment(sketch, "E64", {"start": v(28.07, 10) * mm, "end": v(28.07, 0) * mm});
            skLineSegment(sketch, "E65", {"start": v(2.06, 0) * mm, "end": v(2.06, 7) * mm});
            skLineSegment(sketch, "E66", {"start": v(18.07, 7) * mm, "end": v(2.06, 0) * mm});
            skSolve(sketch);
        }
        {
            var Q0;
            {var subQ4=sQuery(id+"F19.wireOp",EDGE,"E62.top");Q0=makeQuery(id+"F19.imprint","IMPRINT",FACE,{"disambiguationData":[TD([[makeQuery(id+"F19.imprint","IMPRINT",EDGE,{"derivedFrom":subQ4}),1.0]])]});}
            extrude(context, id + "F20", {"entities" : qUnion([Q0]), "operationType" : NewBodyOperationType.ADD, "depth" : 20 * mm});
        }
        {
            var Q0;
            Q0=makeQuery(id+"F5.opExtrude","SWEPT_BODY",BODY,{"disambiguationData":[OSD([sQuery(id+"F0.wireOp",EDGE,"E24"),sQuery(id+"F0.wireOp",EDGE,"E25"),sQuery(id+"F0.wireOp",EDGE,"E36"),sQuery(id+"F0.wireOp",EDGE,"E43"),sQuery(id+"F0.wireOp",EDGE,"E52")])]});
            deleteBodies(context, id + "F21", {"entities" : qUnion([Q0])});
        }
        {
            var Q0;
            Q0=makeQuery(id+"F3.opExtrude","SWEPT_FACE",FACE,{"disambiguationData":[OSD([sQuery(id+"F0.wireOp",EDGE,"E43")])]});
            var sketch = newSketch(context, id + "F22", { "sketchPlane" : qUnion([Q0])});
            skLineSegment(sketch, "E67", {"start": v(-12.37, 10) * mm, "end": v(-2.37, 10) * mm});
            skPoint(sketch, "E67.endSnap0", {"position": v(-12.37, 10) * mm});
            skLineSegment(sketch, "E68", {"start": v(-2.37, 10) * mm, "end": v(-2.37, 13) * mm});
            skLineSegment(sketch, "E69.bottom", {"start": v(-2.37, 13) * mm, "end": v(20.13, 13) * mm});
            skLineSegment(sketch, "E69.top", {"start": v(-2.37, 7) * mm, "end": v(20.13, 7) * mm});
            skLineSegment(sketch, "E69.left", {"start": v(-2.37, 13) * mm, "end": v(-2.37, 7) * mm});
            skLineSegment(sketch, "E69.right", {"start": v(20.13, 13) * mm, "end": v(20.13, 7) * mm});
            skSolve(sketch);
        }
        {
            var Q0;
            Q0 = qSketchRegion(id + "F22", true);
            extrude(context, id + "F23", {"entities" : qUnion([Q0]), "operationType" : NewBodyOperationType.ADD, "depth" : 20 * mm});
        }
    });
